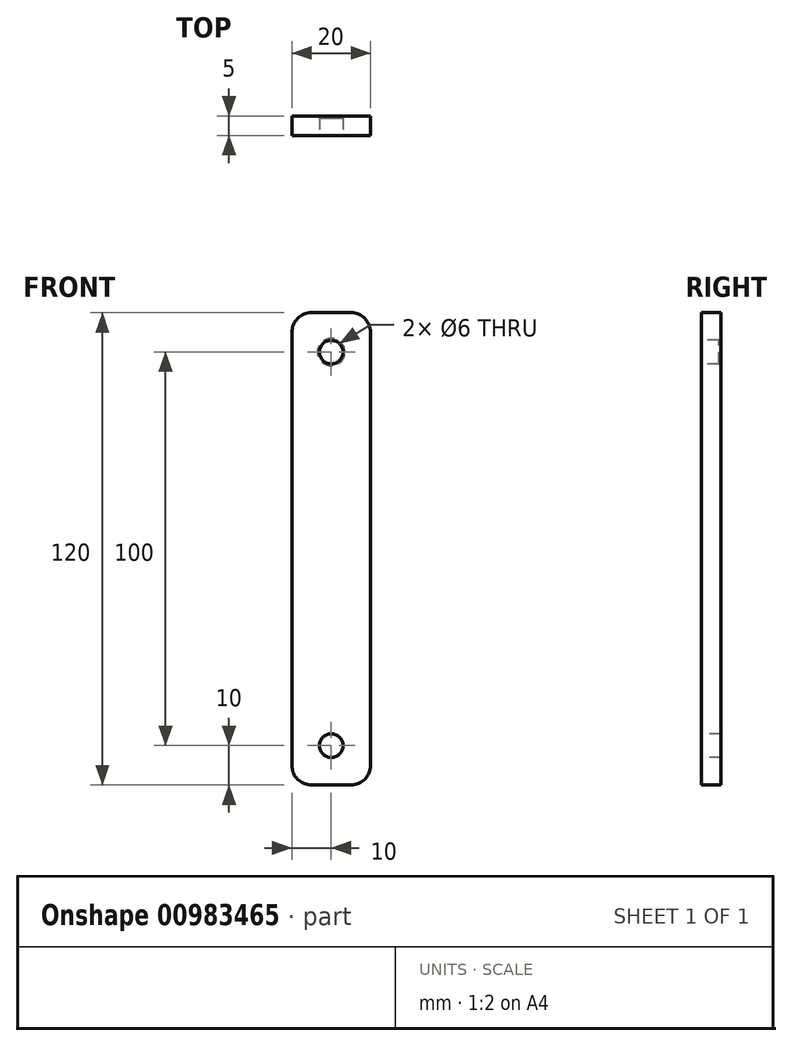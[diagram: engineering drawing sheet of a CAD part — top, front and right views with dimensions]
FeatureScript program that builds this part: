
annotation { "Feature Type Name" : "Feature", "Feature Type Description" : "" }
export const myFeature = defineFeature(function(context is Context, id is Id, definition is map)
    precondition{}
    {
        {
            var Q0;
            Q0=qCreatedBy(makeId("Front.planeOp"),FACE);
            var sketch = newSketch(context, id + "F0", { "sketchPlane" : qUnion([Q0])});
            skLineSegment(sketch, "E0.bottom", {"start": v(0, 0) * mm, "end": v(20, 0) * mm});
            skLineSegment(sketch, "E0.top", {"start": v(0, 120) * mm, "end": v(20, 120) * mm});
            skLineSegment(sketch, "E0.left", {"start": v(0, 0) * mm, "end": v(0, 120) * mm});
            skLineSegment(sketch, "E0.right", {"start": v(20, 0) * mm, "end": v(20, 120) * mm});
            skSolve(sketch);
        }
        {
            var Q0;
            Q0=qSketchRegion(id+"F0",true);
            extrude(context, id + "F1", {"entities" : qUnion([Q0]), "depth" : 5 * mm});
        }
        {
            var Q0;
            Q0=makeQuery(id+"F1.opExtrude","CAP_FACE",FACE,{"disambiguationData":[OSD([sQuery(id+"F0.wireOp",EDGE,"E0.bottom"),sQuery(id+"F0.wireOp",EDGE,"E0.top"),sQuery(id+"F0.wireOp",EDGE,"E0.left"),sQuery(id+"F0.wireOp",EDGE,"E0.right")])],"isStart":false});
            var sketch = newSketch(context, id + "F2", { "sketchPlane" : qUnion([Q0])});
            skCircle(sketch, "E1", {"center": v(10, 110) * mm, "radius": 3 * mm});
            skSolve(sketch);
        }
        {
            var Q0;
            Q0=qSketchRegion(id+"F2",true);
            extrude(context, id + "F3", {"entities" : qUnion([Q0]), "operationType" : NewBodyOperationType.REMOVE, "endBound" : BoundingType.THROUGH_ALL, "oppositeDirection" : true, "depth" : 25 * mm});
        }
        {
            var Q0;
            Q0=makeQuery(id+"F1.opExtrude","CAP_FACE",FACE,{"disambiguationData":[OSD([sQuery(id+"F0.wireOp",EDGE,"E0.bottom"),sQuery(id+"F0.wireOp",EDGE,"E0.top"),sQuery(id+"F0.wireOp",EDGE,"E0.left"),sQuery(id+"F0.wireOp",EDGE,"E0.right")])],"isStart":false});
            var sketch = newSketch(context, id + "F4", { "sketchPlane" : qUnion([Q0])});
            skLineSegment(sketch, "E2", {"start": v(10, 110) * mm, "end": v(10, 10) * mm});
            skSolve(sketch);
        }
        {
            var Q0;
            Q0=sQuery(id+"F4.wireOp",VERTEX,"E2.end");
            var Q1;
            Q1=makeQuery(id+"F1.opExtrude","SWEPT_BODY",BODY,{"disambiguationData":[OSD([sQuery(id+"F0.wireOp",EDGE,"E0.bottom"),sQuery(id+"F0.wireOp",EDGE,"E0.top"),sQuery(id+"F0.wireOp",EDGE,"E0.left"),sQuery(id+"F0.wireOp",EDGE,"E0.right")])]});
            hole(context, id + "F5", {"style" : HoleStyle.SIMPLE, "endStyle" : HoleEndStyle.THROUGH, "holeDiameter" : 6 * mm, "isTappedThrough" : true, "tappedDepth" : 12 * mm, "tapClearance" : 3, "locations" : qUnion([Q0]), "scope" : qUnion([Q1])});
        }
        {
            var Q0;
            Q0=makeQuery(id+"F3.boolean.opBoolean","COPY",EDGE,{"derivedFrom":makeQuery(id+"F3.opExtrude","CAP_EDGE",EDGE,{"disambiguationData":[OSD([sQuery(id+"F2.wireOp",EDGE,"E1")])],"isStart":true})});
            var Q1;
            Q1=makeQuery(id+"F3.boolean.opBoolean","INTERSECT",EDGE,{"derivedFrom":[makeQuery(id+"F1.opExtrude","CAP_FACE",FACE,{"disambiguationData":[OSD([sQuery(id+"F0.wireOp",EDGE,"E0.bottom"),sQuery(id+"F0.wireOp",EDGE,"E0.top"),sQuery(id+"F0.wireOp",EDGE,"E0.left"),sQuery(id+"F0.wireOp",EDGE,"E0.right")])],"isStart":true}),makeQuery(id+"F3.opExtrude","SWEPT_FACE",FACE,{"disambiguationData":[OSD([sQuery(id+"F2.wireOp",EDGE,"E1")])]})]});
            var Q2;
            Q2=makeQuery(id+"F5.hole-0.boolean.opBoolean","INTERSECT",EDGE,{"derivedFrom":[makeQuery(id+"F1.opExtrude","CAP_FACE",FACE,{"disambiguationData":[OSD([sQuery(id+"F0.wireOp",EDGE,"E0.bottom"),sQuery(id+"F0.wireOp",EDGE,"E0.top"),sQuery(id+"F0.wireOp",EDGE,"E0.left"),sQuery(id+"F0.wireOp",EDGE,"E0.right")])],"isStart":true}),makeQuery(id+"F5.hole-0.opRevolve","SWEPT_FACE",FACE,{"disambiguationData":[OSD([sQuery(id+"F5.hole-0.sketch.wireOp",EDGE,"core_line_2")])]})]});
            var Q3;
            Q3=makeQuery(id+"F5.hole-0.boolean.opBoolean","COPY",EDGE,{"derivedFrom":makeQuery(id+"F5.hole-0.opRevolve","SWEPT_EDGE",EDGE,{"disambiguationData":[OSD([sQuery(id+"F5.hole-0.sketch.wireOp",EDGE,"core_line_2"),sQuery(id+"F5.hole-0.sketch.wireOp",EDGE,"core_line_3")])]})});
            var Q4;
            Q4=makeQuery(id+"FU6Ed1FcUmWV3el_1.hole-1.boolean.opBoolean","COPY",EDGE,{"derivedFrom":makeQuery(id+"FU6Ed1FcUmWV3el_1.hole-1.opRevolve","SWEPT_EDGE",EDGE,{"disambiguationData":[OSD([sQuery(id+"FU6Ed1FcUmWV3el_1.hole-1.sketch.wireOp",EDGE,"core_line_2"),sQuery(id+"FU6Ed1FcUmWV3el_1.hole-1.sketch.wireOp",EDGE,"core_line_3")])]})});
            var Q5;
            Q5=makeQuery(id+"FU6Ed1FcUmWV3el_1.hole-1.boolean.opBoolean","INTERSECT",EDGE,{"derivedFrom":[makeQuery(id+"F1.opExtrude","CAP_FACE",FACE,{"disambiguationData":[OSD([sQuery(id+"F0.wireOp",EDGE,"E0.bottom"),sQuery(id+"F0.wireOp",EDGE,"E0.top"),sQuery(id+"F0.wireOp",EDGE,"E0.left"),sQuery(id+"F0.wireOp",EDGE,"E0.right")])],"isStart":true}),makeQuery(id+"FU6Ed1FcUmWV3el_1.hole-1.opRevolve","SWEPT_FACE",FACE,{"disambiguationData":[OSD([sQuery(id+"FU6Ed1FcUmWV3el_1.hole-1.sketch.wireOp",EDGE,"core_line_2")])]})]});
            var Q6;
            Q6=makeQuery(id+"FU6Ed1FcUmWV3el_1.hole-0.boolean.opBoolean","COPY",EDGE,{"derivedFrom":makeQuery(id+"FU6Ed1FcUmWV3el_1.hole-0.opRevolve","SWEPT_EDGE",EDGE,{"disambiguationData":[OSD([sQuery(id+"FU6Ed1FcUmWV3el_1.hole-0.sketch.wireOp",EDGE,"core_line_2"),sQuery(id+"FU6Ed1FcUmWV3el_1.hole-0.sketch.wireOp",EDGE,"core_line_3")])]})});
            var Q7;
            Q7=makeQuery(id+"FU6Ed1FcUmWV3el_1.hole-0.boolean.opBoolean","INTERSECT",EDGE,{"derivedFrom":[makeQuery(id+"F1.opExtrude","CAP_FACE",FACE,{"disambiguationData":[OSD([sQuery(id+"F0.wireOp",EDGE,"E0.bottom"),sQuery(id+"F0.wireOp",EDGE,"E0.top"),sQuery(id+"F0.wireOp",EDGE,"E0.left"),sQuery(id+"F0.wireOp",EDGE,"E0.right")])],"isStart":true}),makeQuery(id+"FU6Ed1FcUmWV3el_1.hole-0.opRevolve","SWEPT_FACE",FACE,{"disambiguationData":[OSD([sQuery(id+"FU6Ed1FcUmWV3el_1.hole-0.sketch.wireOp",EDGE,"core_line_2")])]})]});
            chamfer(context, id + "F6", {"entities" : qUnion([Q0, Q1, Q2, Q3, Q4, Q5, Q6, Q7]), "width" : 0.5 * mm, "tangentPropagation" : true});
        }
        {
            var Q0;
            Q0=makeQuery(id+"F1.opExtrude","SWEPT_EDGE",EDGE,{"disambiguationData":[OSD([sQuery(id+"F0.wireOp",EDGE,"E0.top"),sQuery(id+"F0.wireOp",EDGE,"E0.right")])]});
            var Q1;
            Q1=makeQuery(id+"F1.opExtrude","SWEPT_EDGE",EDGE,{"disambiguationData":[OSD([sQuery(id+"F0.wireOp",EDGE,"E0.top"),sQuery(id+"F0.wireOp",EDGE,"E0.left")])]});
            var Q2;
            Q2=makeQuery(id+"F1.opExtrude","SWEPT_EDGE",EDGE,{"disambiguationData":[OSD([sQuery(id+"F0.wireOp",EDGE,"E0.bottom"),sQuery(id+"F0.wireOp",EDGE,"E0.right")])]});
            var Q3;
            Q3=makeQuery(id+"F1.opExtrude","SWEPT_EDGE",EDGE,{"disambiguationData":[OSD([sQuery(id+"F0.wireOp",EDGE,"E0.bottom"),sQuery(id+"F0.wireOp",EDGE,"E0.left")])]});
            fillet(context, id + "F7", {"entities" : qUnion([Q0, Q1, Q2, Q3]), "radius" : 5 * mm, "tangentPropagation" : true, "allowEdgeOverflow" : false});
        }
    });
